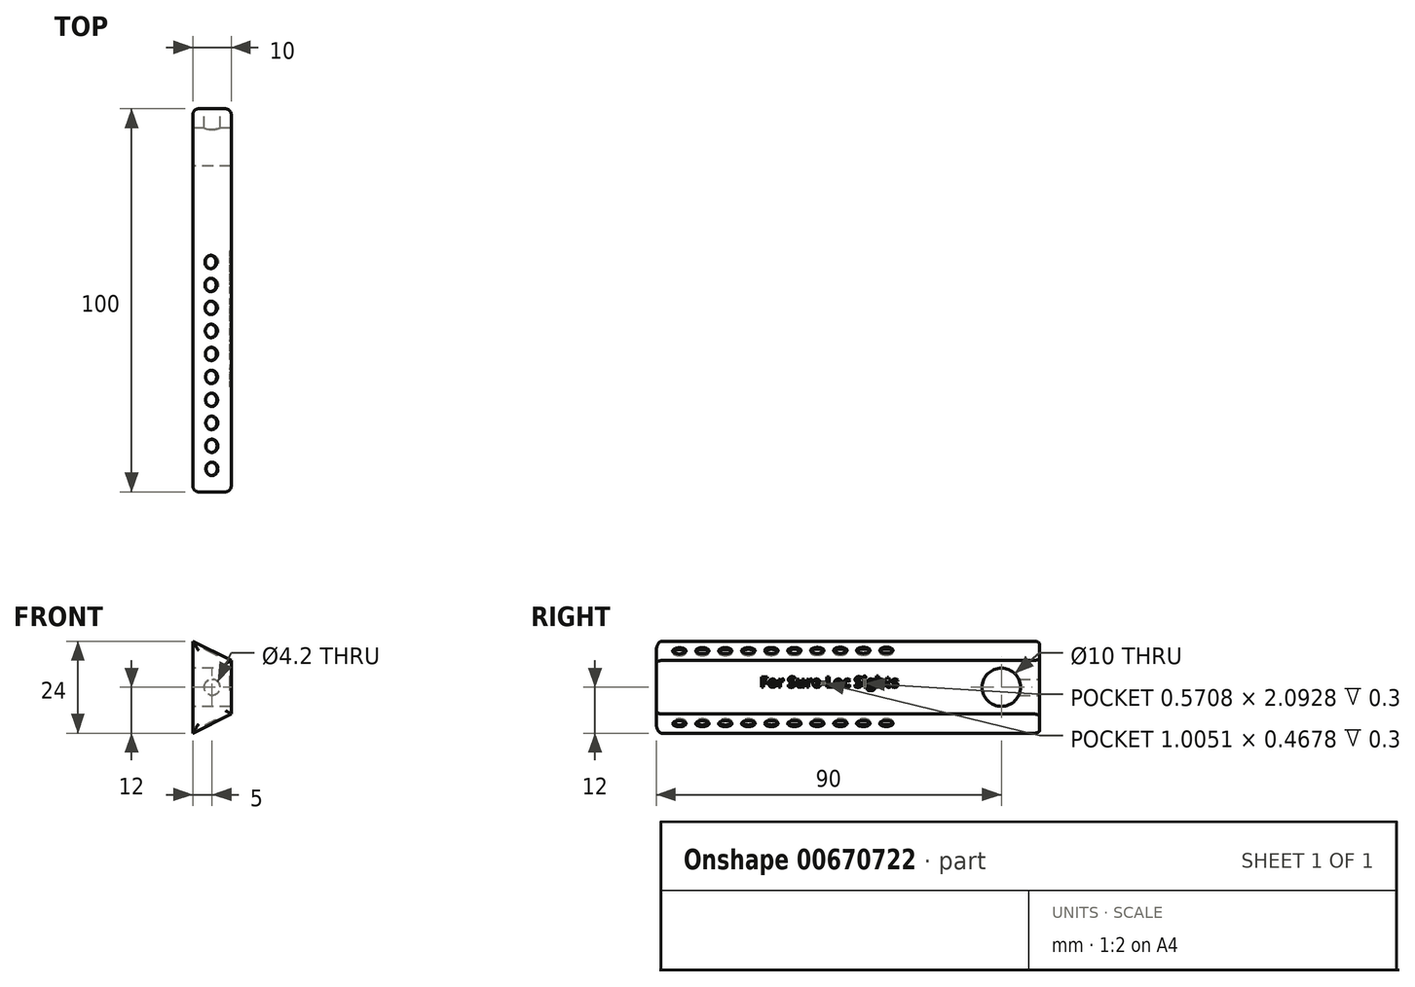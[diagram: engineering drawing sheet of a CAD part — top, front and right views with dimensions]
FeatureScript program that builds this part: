
annotation { "Feature Type Name" : "Feature", "Feature Type Description" : "" }
export const myFeature = defineFeature(function(context is Context, id is Id, definition is map)
    precondition{}
    {
        {
            var Q0;
            Q0=qCreatedBy(makeId("Right.planeOp"),FACE);
            var sketch = newSketch(context, id + "F0", { "sketchPlane" : qUnion([Q0])});
            skLineSegment(sketch, "E0.bottom", {"start": v(50, 12) * mm, "end": v(-50, 12) * mm});
            skLineSegment(sketch, "E0.top", {"start": v(50, -12) * mm, "end": v(-50, -12) * mm});
            skLineSegment(sketch, "E0.left", {"start": v(50, 12) * mm, "end": v(50, -12) * mm});
            skLineSegment(sketch, "E0.right", {"start": v(-50, 12) * mm, "end": v(-50, -12) * mm});
            skPoint(sketch, "E0.middle", {"position": v(0, 0) * mm});
            skLineSegment(sketch, "E1.left", {"start": v(50, 7) * mm, "end": v(30, -7) * mm});
            skLineSegment(sketch, "E1.right", {"start": v(-30, 7) * mm, "end": v(-50, -7) * mm});
            skSolve(sketch);
        }
        {
            var Q0;
            Q0 = qSketchRegion(id + "F0", true);
            extrude(context, id + "F1", {"entities" : qUnion([Q0]), "endBound" : BoundingType.SYMMETRIC, "depth" : 10 * mm, "offsetDistance" : 25 * mm});
        }
        {
            var Q0;
            Q0=makeQuery(id+"F1.opExtrude","SWEPT_FACE",FACE,{"disambiguationData":[OSD([sQuery(id+"F0.wireOp",EDGE,"E0.left"),sQuery(id+"F0.wireOp",EDGE,"E1.left")])]});
            var sketch = newSketch(context, id + "F2", { "sketchPlane" : qUnion([Q0])});
            skLineSegment(sketch, "E2", {"start": v(-5, 0) * mm, "end": v(-5, 7) * mm});
            skLineSegment(sketch, "E3", {"start": v(-5, 7) * mm, "end": v(-5, 0) * mm});
            skLineSegment(sketch, "E4", {"start": v(-5, 0) * mm, "end": v(-5, -7) * mm});
            skLineSegment(sketch, "E5", {"start": v(-5, 7) * mm, "end": v(5, 12) * mm});
            skLineSegment(sketch, "E6", {"start": v(5, 12) * mm, "end": v(-5, 12) * mm});
            skLineSegment(sketch, "E7", {"start": v(-5, 12) * mm, "end": v(-5, 7) * mm});
            skLineSegment(sketch, "E8", {"start": v(-5, -7) * mm, "end": v(5, -12) * mm});
            skLineSegment(sketch, "E9", {"start": v(5, -12) * mm, "end": v(-5, -12) * mm});
            skLineSegment(sketch, "E10", {"start": v(-5, -12) * mm, "end": v(-5, -7) * mm});
            skSolve(sketch);
        }
        {
            var Q0;
            Q0=makeQuery(id+"F2.imprint","IMPRINT",FACE,{"disambiguationData":[TD([[makeQuery(id+"F2.imprint","IMPRINT",EDGE,{"derivedFrom":sQuery(id+"F2.wireOp",EDGE,"E5")}),1.0]])]});
            var Q1;
            Q1=makeQuery(id+"F2.imprint","IMPRINT",FACE,{"disambiguationData":[TD([[makeQuery(id+"F2.imprint","IMPRINT",EDGE,{"derivedFrom":sQuery(id+"F2.wireOp",EDGE,"E8")}),-1.0]])]});
            extrude(context, id + "F3", {"entities" : qUnion([Q0, Q1]), "operationType" : NewBodyOperationType.REMOVE, "endBound" : BoundingType.THROUGH_ALL, "oppositeDirection" : true, "depth" : 25 * mm, "offsetDistance" : 25 * mm});
        }
        {
            var Q0;
            Q0=makeQuery(id+"F1.opExtrude","SWEPT_FACE",FACE,{"disambiguationData":[OSD([sQuery(id+"F0.wireOp",EDGE,"E0.left"),sQuery(id+"F0.wireOp",EDGE,"E1.left")])]});
            var sketch = newSketch(context, id + "F4", { "sketchPlane" : qUnion([Q0])});
            skPoint(sketch, "E11", {"position": v(0, 0) * mm});
            skSolve(sketch);
        }
        {
            var Q0;
            Q0=sQuery(id+"F4.wireOp",VERTEX,"E11");
            var Q1;
            Q1=makeQuery(id+"F1.opExtrude","SWEPT_BODY",BODY,{"disambiguationData":[OSD([sQuery(id+"F0.wireOp",EDGE,"E0.bottom"),sQuery(id+"F0.wireOp",EDGE,"E0.top"),sQuery(id+"F0.wireOp",EDGE,"E0.left"),sQuery(id+"F0.wireOp",EDGE,"E0.right"),sQuery(id+"F0.wireOp",EDGE,"E1.left"),sQuery(id+"F0.wireOp",EDGE,"E1.right")])]});
            hole(context, id + "F5", {"style" : HoleStyle.SIMPLE, "endStyle" : HoleEndStyle.BLIND, "standardTappedOrClearance" : lookupTablePath({ "standard" : "ISO", "engagement" : "75%", "pitch" : "0.8 mm", "size" : "M5", "type" : "Tapped" }), "standardBlindInLast" : lookupTablePath({ "standard" : "ISO", "engagement" : "75%", "pitch" : "0.8 mm", "size" : "M5", "type" : "Tapped" }), "holeDiameter" : 4.2 * mm, "majorDiameter" : 5 * mm, "showTappedDepth" : true, "holeDepth" : 10 * mm, "isTappedThrough" : true, "tappedDepth" : 7.6 * mm, "tapClearance" : 3, "startFromSketch" : true, "locations" : qUnion([Q0]), "scope" : qUnion([Q1])});
        }
        {
            var Q0;
            Q0=makeQuery(id+"F1.opExtrude","CAP_FACE",FACE,{"disambiguationData":[OSD([sQuery(id+"F0.wireOp",EDGE,"E0.bottom"),sQuery(id+"F0.wireOp",EDGE,"E0.top"),sQuery(id+"F0.wireOp",EDGE,"E0.left"),sQuery(id+"F0.wireOp",EDGE,"E0.right"),sQuery(id+"F0.wireOp",EDGE,"E1.left"),sQuery(id+"F0.wireOp",EDGE,"E1.right")])],"isStart":true});
            var sketch = newSketch(context, id + "F6", { "sketchPlane" : qUnion([Q0])});
            skPoint(sketch, "E12", {"position": v(-40, 0) * mm});
            skCircle(sketch, "E13", {"center": v(-40, 0) * mm, "radius": 5 * mm});
            skSolve(sketch);
        }
        {
            var Q0;
            Q0=makeQuery(id+"F6.imprint","IMPRINT",FACE,{"disambiguationData":[TD([[makeQuery(id+"F6.imprint","IMPRINT",EDGE,{"derivedFrom":sQuery(id+"F6.wireOp",EDGE,"E13")}),1.0]])]});
            extrude(context, id + "F7", {"entities" : qUnion([Q0]), "operationType" : NewBodyOperationType.REMOVE, "endBound" : BoundingType.THROUGH_ALL, "oppositeDirection" : true, "depth" : 25 * mm, "offsetDistance" : 25 * mm});
        }
        {
            var Q0;
            Q0=makeQuery(id+"F3.boolean.opBoolean","COPY",FACE,{"derivedFrom":makeQuery(id+"F3.opExtrude","SWEPT_FACE",FACE,{"disambiguationData":[OSD([sQuery(id+"F2.wireOp",EDGE,"E5")])]})});
            var sketch = newSketch(context, id + "F8", { "sketchPlane" : qUnion([Q0])});
            skPoint(sketch, "E14", {"position": v(-4.25, -44) * mm});
            skPoint(sketch, "E14.positionSnap0", {"position": v(-4.25, -50) * mm});
            skCircle(sketch, "E15", {"center": v(-4.25, -44) * mm, "radius": 1.75 * mm});
            skCircle(sketch, "E16.1.0.0", {"center": v(-4.29, -38) * mm, "radius": 1.75 * mm});
            skCircle(sketch, "E16.2.0.0", {"center": v(-4.32, -32) * mm, "radius": 1.75 * mm});
            skCircle(sketch, "E16.3.0.0", {"center": v(-4.36, -26) * mm, "radius": 1.75 * mm});
            skCircle(sketch, "E16.4.0.0", {"center": v(-4.4, -20) * mm, "radius": 1.75 * mm});
            skCircle(sketch, "E16.5.0.0", {"center": v(-4.43, -14) * mm, "radius": 1.75 * mm});
            skLineSegment(sketch, "E16.direction1", {"start": v(-4.25, -44) * mm, "end": v(-4.29, -38) * mm, "construction": true});
            skCircle(sketch, "E17.0.6.0", {"center": v(-4.47, -8) * mm, "radius": 1.75 * mm});
            skCircle(sketch, "E17.0.7.0", {"center": v(-4.5, -2) * mm, "radius": 1.75 * mm});
            skCircle(sketch, "E17.0.8.0", {"center": v(-4.54, 4) * mm, "radius": 1.75 * mm});
            skCircle(sketch, "E17.0.9.0", {"center": v(-4.58, 10) * mm, "radius": 1.75 * mm});
            skSolve(sketch);
        }
        {
            var Q0;
            Q0 = qSketchRegion(id + "F8", true);
            extrude(context, id + "F9", {"entities" : qUnion([Q0]), "operationType" : NewBodyOperationType.REMOVE, "oppositeDirection" : true, "depth" : 0.5 * mm, "offsetDistance" : 25 * mm});
        }
        {
            var Q0;
            Q0=makeQuery(id+"F3.boolean.opBoolean","COPY",FACE,{"derivedFrom":makeQuery(id+"F3.opExtrude","SWEPT_FACE",FACE,{"disambiguationData":[OSD([sQuery(id+"F2.wireOp",EDGE,"E8")])]})});
            var sketch = newSketch(context, id + "F10", { "sketchPlane" : qUnion([Q0])});
            skPoint(sketch, "E18", {"position": v(-4.25, 44) * mm});
            skPoint(sketch, "E18.positionSnap0", {"position": v(-4.25, 50) * mm});
            skCircle(sketch, "E19", {"center": v(-4.25, 44) * mm, "radius": 1.75 * mm});
            skCircle(sketch, "E20.1.0.0", {"center": v(-4.24, 38) * mm, "radius": 1.75 * mm});
            skCircle(sketch, "E20.2.0.0", {"center": v(-4.23, 32) * mm, "radius": 1.75 * mm});
            skCircle(sketch, "E20.3.0.0", {"center": v(-4.22, 26) * mm, "radius": 1.75 * mm});
            skCircle(sketch, "E20.4.0.0", {"center": v(-4.2, 20) * mm, "radius": 1.75 * mm});
            skCircle(sketch, "E20.5.0.0", {"center": v(-4.2, 14) * mm, "radius": 1.75 * mm});
            skLineSegment(sketch, "E20.direction1", {"start": v(-4.25, 44) * mm, "end": v(-4.24, 38) * mm, "construction": true});
            skCircle(sketch, "E21.0.6.0", {"center": v(-4.18, 8) * mm, "radius": 1.75 * mm});
            skCircle(sketch, "E21.0.7.0", {"center": v(-4.17, 2) * mm, "radius": 1.75 * mm});
            skCircle(sketch, "E21.0.8.0", {"center": v(-4.16, -4) * mm, "radius": 1.75 * mm});
            skCircle(sketch, "E21.0.9.0", {"center": v(-4.15, -10) * mm, "radius": 1.75 * mm});
            skSolve(sketch);
        }
        {
            var Q0;
            Q0 = qSketchRegion(id + "F10", true);
            extrude(context, id + "F11", {"entities" : qUnion([Q0]), "operationType" : NewBodyOperationType.REMOVE, "oppositeDirection" : true, "depth" : 0.5 * mm, "offsetDistance" : 25 * mm});
        }
        {
            var Q0;
            Q0=makeQuery(id+"F1.opExtrude","CAP_FACE",FACE,{"disambiguationData":[OSD([sQuery(id+"F0.wireOp",EDGE,"E0.bottom"),sQuery(id+"F0.wireOp",EDGE,"E0.top"),sQuery(id+"F0.wireOp",EDGE,"E0.left"),sQuery(id+"F0.wireOp",EDGE,"E0.right"),sQuery(id+"F0.wireOp",EDGE,"E1.left"),sQuery(id+"F0.wireOp",EDGE,"E1.right")])],"isStart":false});
            var sketch = newSketch(context, id + "F12", { "sketchPlane" : qUnion([Q0])});
            skText(sketch, "E22", { "text": "For Sure-Loc Sights", "fontName": "OpenSans-Bold.ttf"});
            const initialGuessF12  = {"E22": [-0.02295, 0, 1, 0, 0.00276]};
            skSetInitialGuess(sketch, initialGuessF12);
            skSolve(sketch);
        }
        {
            var Q0;
            Q0 = qSketchRegion(id + "F12", true);
            extrude(context, id + "F13", {"entities" : qUnion([Q0]), "operationType" : NewBodyOperationType.REMOVE, "oppositeDirection" : true, "depth" : 0.3 * mm, "offsetDistance" : 25 * mm});
        }
        {
            var Q0;
            Q0=makeQuery(id+"F3.boolean.opBoolean","COPY",EDGE,{"derivedFrom":makeQuery(id+"F3.opExtrude","SWEPT_EDGE",EDGE,{"disambiguationData":[OSD([sQuery(id+"F2.wireOp",EDGE,"E3"),sQuery(id+"F2.wireOp",EDGE,"E5"),sQuery(id+"F2.wireOp",EDGE,"E7")])]})});
            var Q1;
            Q1=makeQuery(id+"F3.boolean.opBoolean","COPY",EDGE,{"derivedFrom":makeQuery(id+"F3.opExtrude","SWEPT_EDGE",EDGE,{"disambiguationData":[OSD([sQuery(id+"F2.wireOp",EDGE,"E4"),sQuery(id+"F2.wireOp",EDGE,"E8"),sQuery(id+"F2.wireOp",EDGE,"E10")])]})});
            var Q2;
            Q2=makeQuery(id+"F3.boolean.opBoolean","INTERSECT",EDGE,{"derivedFrom":[makeQuery(id+"F1.opExtrude","SWEPT_FACE",FACE,{"disambiguationData":[OSD([sQuery(id+"F0.wireOp",EDGE,"E0.right"),sQuery(id+"F0.wireOp",EDGE,"E1.right")])]}),makeQuery(id+"F3.opExtrude","SWEPT_FACE",FACE,{"disambiguationData":[OSD([sQuery(id+"F2.wireOp",EDGE,"E5")])]})]});
            var Q3;
            Q3=makeQuery(id+"F1.opExtrude","CAP_EDGE",EDGE,{"disambiguationData":[OSD([sQuery(id+"F0.wireOp",EDGE,"E0.right"),sQuery(id+"F0.wireOp",EDGE,"E1.right")])],"isStart":false});
            var Q4;
            Q4=makeQuery(id+"F3.boolean.opBoolean","INTERSECT",EDGE,{"derivedFrom":[makeQuery(id+"F1.opExtrude","SWEPT_FACE",FACE,{"disambiguationData":[OSD([sQuery(id+"F0.wireOp",EDGE,"E0.right"),sQuery(id+"F0.wireOp",EDGE,"E1.right")])]}),makeQuery(id+"F3.opExtrude","SWEPT_FACE",FACE,{"disambiguationData":[OSD([sQuery(id+"F2.wireOp",EDGE,"E8")])]})]});
            var Q5;
            Q5=makeQuery(id+"F3.boolean.opBoolean","COPY",EDGE,{"derivedFrom":makeQuery(id+"F3.opExtrude","CAP_EDGE",EDGE,{"disambiguationData":[OSD([sQuery(id+"F2.wireOp",EDGE,"E8")])],"isStart":true})});
            var Q6;
            Q6=makeQuery(id+"F3.boolean.opBoolean","COPY",EDGE,{"derivedFrom":makeQuery(id+"F3.opExtrude","CAP_EDGE",EDGE,{"disambiguationData":[OSD([sQuery(id+"F2.wireOp",EDGE,"E5")])],"isStart":true})});
            var Q7;
            Q7=makeQuery(id+"F1.opExtrude","CAP_EDGE",EDGE,{"disambiguationData":[OSD([sQuery(id+"F0.wireOp",EDGE,"E0.left"),sQuery(id+"F0.wireOp",EDGE,"E1.left")])],"isStart":false});
            var Q8;
            Q8=makeQuery(id+"F1.opExtrude","CAP_EDGE",EDGE,{"disambiguationData":[OSD([sQuery(id+"F0.wireOp",EDGE,"E0.left"),sQuery(id+"F0.wireOp",EDGE,"E1.left")])],"isStart":true});
            var Q9;
            Q9=makeQuery(id+"F1.opExtrude","CAP_EDGE",EDGE,{"disambiguationData":[OSD([sQuery(id+"F0.wireOp",EDGE,"E0.right"),sQuery(id+"F0.wireOp",EDGE,"E1.right")])],"isStart":true});
            fillet(context, id + "F14", {"entities" : qUnion([Q0, Q1, Q2, Q3, Q4, Q5, Q6, Q7, Q8, Q9]), "radius" : 1.5 * mm, "tangentPropagation" : true, "allowEdgeOverflow" : false});
        }
    });
